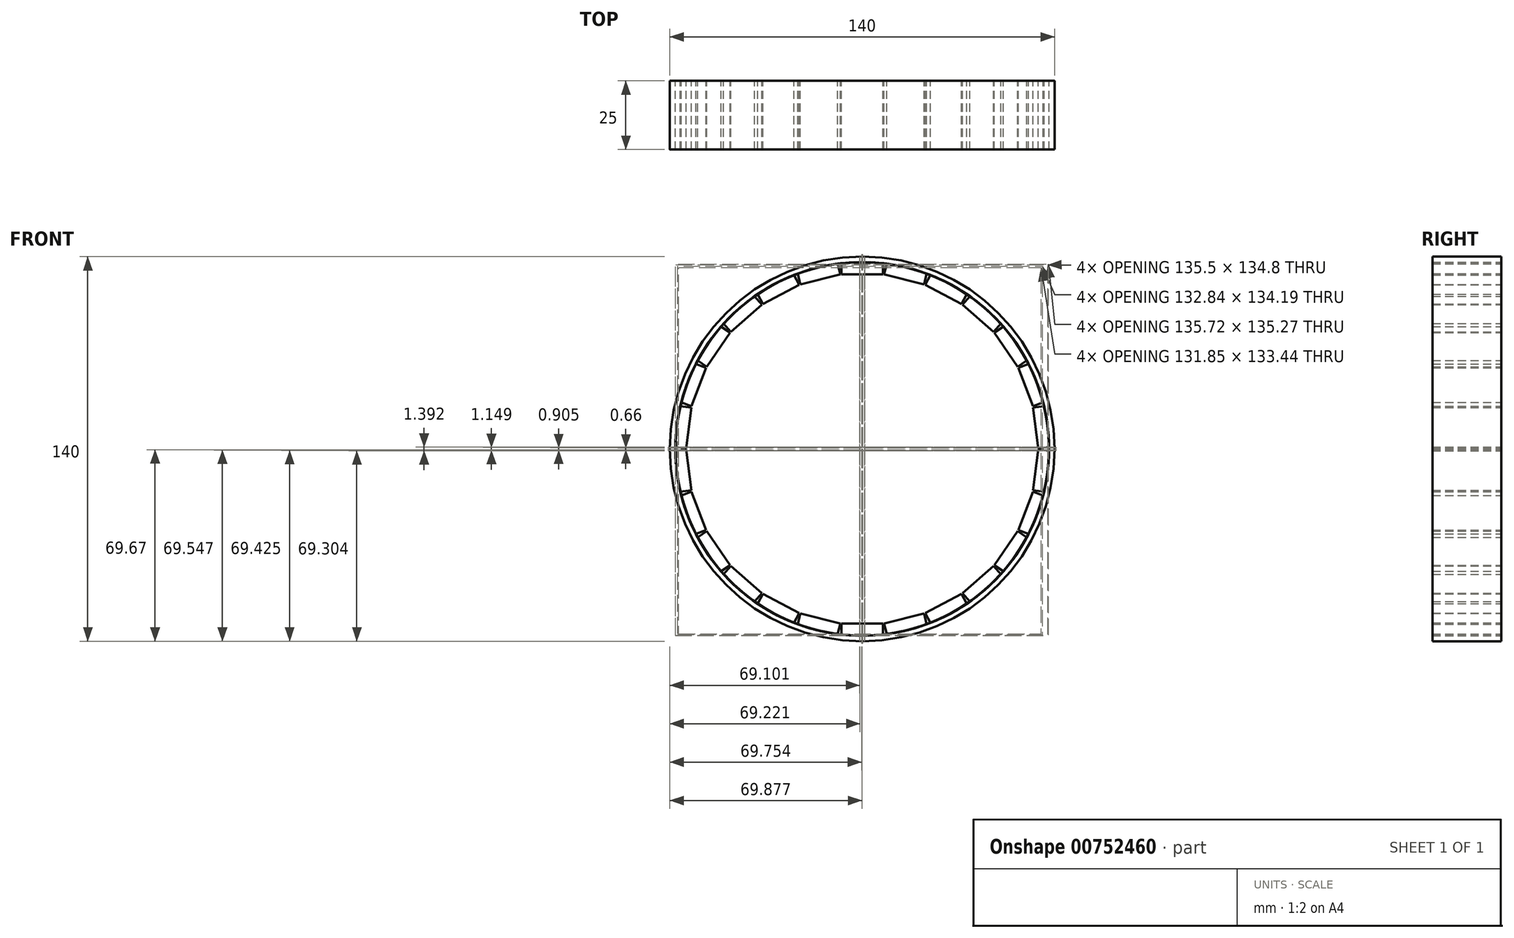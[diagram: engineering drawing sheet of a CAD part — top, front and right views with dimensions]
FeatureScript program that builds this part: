
annotation { "Feature Type Name" : "Feature", "Feature Type Description" : "" }
export const myFeature = defineFeature(function(context is Context, id is Id, definition is map)
    precondition{}
    {
        {
            var Q0;
            Q0=qCreatedBy(makeId("Front.planeOp"),FACE);
            var sketch = newSketch(context, id + "F0", { "sketchPlane" : qUnion([Q0])});
            skCircle(sketch, "E0", {"center": v(0, 0) * mm, "radius": 68 * mm});
            skCircle(sketch, "E1", {"center": v(0, 0) * mm, "radius": 70 * mm});
            skLineSegment(sketch, "E2", {"start": v(0, 0) * mm, "end": v(0, 68) * mm});
            skLineSegment(sketch, "E3", {"start": v(7.5, 67.59) * mm, "end": v(7.5, 63.59) * mm});
            skLineSegment(sketch, "E4.MirrorCS", {"start": v(-7.5, 67.59) * mm, "end": v(-7.5, 63.59) * mm});
            skLineSegment(sketch, "E5", {"start": v(-7.5, 63.59) * mm, "end": v(7.5, 63.59) * mm});
            skSolve(sketch);
        }
        {
            var Q0;
            Q0 = qSketchRegion(id + "F0", true);
            var Q1;
            {var subQ3=sQuery(id+"F0.wireOp",EDGE,"E4.MirrorCS");Q1=makeQuery(id+"F0.imprint","IMPRINT",FACE,{"disambiguationData":[TD([[makeQuery(id+"F0.imprint","IMPRINT",EDGE,{"derivedFrom":subQ3}),1.0]])]});}
            var Q2;
            {var subQ3=sQuery(id+"F0.wireOp",EDGE,"E3");Q2=makeQuery(id+"F0.imprint","IMPRINT",FACE,{"disambiguationData":[TD([[makeQuery(id+"F0.imprint","IMPRINT",EDGE,{"derivedFrom":subQ3}),-1.0]])]});}
            extrude(context, id + "F1", {"entities" : qUnion([Q0, Q1, Q2]), "depth" : 25 * mm, "offsetDistance" : 25 * mm});
        }
        {
            var Q0;
            Q0=makeQuery(id+"F1.opExtrude","SWEPT_BODY",BODY,{"disambiguationData":[OSD([sQuery(id+"F0.wireOp",EDGE,"E0"),sQuery(id+"F0.wireOp",EDGE,"E1"),sQuery(id+"F0.wireOp",EDGE,"E3"),sQuery(id+"F0.wireOp",EDGE,"E4.MirrorCS"),sQuery(id+"F0.wireOp",EDGE,"E5")])]});
            var Q1;
            Q1=makeQuery(id+"F1.opExtrude","SWEPT_FACE",FACE,{"disambiguationData":[OSD([sQuery(id+"F0.wireOp",EDGE,"E0")])]});
            circularPattern(context, id + "F2", {"entities" : qUnion([Q0]), "axis" : qUnion([Q1]), "angle" : 360 * degree, "instanceCount" : 26, "equalSpace" : true});
        }
    });
